# Revit family: IS_Conca_A7375_BIM_GB
name_source: partatom
category: Plumbing Fixtures
revit_build: Autodesk Revit 2017 (Build: 20160225_1515(x64)
units: mm (PartAtom-declared; Revit-internal decimal feet)

## family parameters
Always vertical = No
Cut with Voids When Loaded = No
OmniClass Number = 23.45.55.17
OmniClass Title = Mixing Faucets
Part Type = Normal
Room Calculation Point = No
Round Connector Dimension = Use Diameter
Shared = No
Work Plane-Based = No

## types (4) — shared parameters
Accessories = https://www.idealspec.co.uk
AreaUnits = millimeters
AssetType = Fixed
BIMobject category = Sanitary: Taps & Mixer
BarCode = 3800861085782
Brand = Ideal Standard
Brand url = http://www.idealstandard.co.uk
ConnectionType = Plumbing
CurrencyUnit = £
CurrentRevision = 1
Date of publishing = 22/09/2020
Edition number = 1
ExpectedLife = 30
FaucetFunction = UNSET
FaucetOperation = OTHER
FaucetType = OTHER
FlushRate = 0.00 m³
GTIN code = https://3800861085782
Help = https://www.idealspec.co.uk
IFC Classification = Sanitary Terminal
IfcExportAs = IfcValveType
IfcExportType = FAUCET
Installation instructions = https://www.idealspec.co.uk
InstallationInstructions = https://www.idealspec.co.uk
IsBuiltIn = No
IsHighPressure = No
IsSingleFlush = No
LinearUnits = millimeters
MaintenanceInformation = https://www.idealspec.co.uk
Manufacturer = Ideal Standard (UK) Ltd
Manufacturer name = Ideal Standard
ManufacturerURL = https://www.idealspec.co.uk
Material = Brass
Material main = Brass
NettWeight = 1,46 KG
NominalDepth = 82 mm
NominalHeight = 197 mm
NominalLength = 82 mm
NominalWidth = 163 mm  [stored 0.534777 ft]
Product Guid = 17384bdf-9aea-46d6-8c05-e0d8ab46731d
Product SKU = A7375
Product certification = https://www.idealspec.co.uk
Product data url = https://bimobject.com
Product family = Conca
Product group = BATH-SHOWER MIXERS
Product name = CONCA BSH MXR BIN DVGW KIT2/EASYB BR GUN
Product url = https://www.idealstandard.co.uk
ProductInformation = https://www.idealspec.co.uk
QR code = http://bimobject.com
Shape = Cylindrical
Size = 163 x 82 x 197 mm
Space = Internal
SpareParts = https://fastpart-spares.co.uk
Technical description = https://www.idealspec.co.uk
TestPressure = 10 Bar
UNSPSC Code = 301815
URL = https://www.idealspec.co.uk
Uniclass 1.4 Code = L725111
Uniclass 1.4 Description = Mixer taps
Uniclass2015Version = v1.1
Version = 1
VolumeUnits = Litres
WRASURL = https://www.wras.co.uk
WarrantyDescription = Manufacturers Warranty
WarrantyDurationParts = 5
WarrantyDurationUnit = year
WarrantyGuarantorParts = https://www.idealspec.co.uk
zero-valued in all types: FlushingRate, InletConnectionSize, MaterialThickness, OutletConnectionSize

## per-type parameters (varying)
| type | BIMObjectName | Color | Description | Features | Finish | MainColor | Model | ModelNumber | ModelReference | NBS Reference Code | NBS Reference Description | Name | Uniclass 2.0 Code | Uniclass 2.0 Description | Uniclass 2015 Code | Uniclass 2015 Name | Uniclass2015Code | Uniclass2015Title | Uniformat II Code | Uniformat II Description |
| A7375AA - CONCA BSH MXR BIN DVGW KIT2/EASY-BOX CHR | IS_IdealStandard_BathTaps_Conca_A7375 | Chrome | Conca Single Lever built in bath shower mixer - With additional back-flow prevention on second outlet. Requires built in kit A1000NU and a suitable outlet. | Single lever built in bath shower mixer - With additional back-flow prevention on second outlet. Requires built in kit A1000NU and a suitable outlet. | Chrome | Chrome | A7375AA | A7375AA | Single lever built in bath shower mixer - With additional back-flow prevention on second outlet. Requires built in kit A1000NU and a suitable outlet. | 45-35-70/315 | Water supply fittings for baths | BathTaps_Conca_A7375_IdealStandard | Pr_40_30_96_09 | Bath Taps | Pr_40_20_87_09 | Bath taps | Pr_40_20_87_09 | Bath taps | Pr_40_30_96_09 | Bath Taps |
| A7375A2 - CONCA BSH MXR BIN DVGW KIT2/EASYB BR GOLD | IS_IdealStandard_ShowerManualWaterSupplySets_Conca_A7375 | Brushed gold | Conca Single Lever built in shower mixer - Requires built in kit A1300NU and a suitable outlet. | Single lever built in shower mixer - Requires built in kit A1300NU and a suitable outlet. | Brushed gold | Brushed gold | A7375A2 | A7375A2 | Single lever built in shower mixer - Requires built in kit A1300NU and a suitable outlet. | 45-35-70/335 | Shower mixers | ShowerManualWaterSupplySets_Conca_A7375_IdealStandard | Pr_40_30_96_78 | Shower Manual Water Supply Sets | Pr_40_20_87_78 | Shower manual water supply sets | Pr_40_20_87_78 | Shower manual water supply sets | Pr_40_30_96_78 | Shower Manual Water Supply Sets |
| A7375A5 - CONCA BSH MXR BIN DVGW KIT2/EASYB M GREY | IS_IdealStandard_ShowerManualWaterSupplySets_Conca_A7375 | Brushed Gun metal | Conca Single Lever built in shower mixer - Requires built in kit A1300NU and a suitable outlet. | Single lever built in shower mixer - Requires built in kit A1300NU and a suitable outlet. | Brushed Gun metal | Brushed Gun metal | A7375A5 | A7375A5 | Single lever built in shower mixer - Requires built in kit A1300NU and a suitable outlet. | 45-35-70/335 | Shower mixers | ShowerManualWaterSupplySets_Conca_A7375_IdealStandard | Pr_40_30_96_78 | Shower Manual Water Supply Sets | Pr_40_20_87_78 | Shower manual water supply sets | Pr_40_20_87_78 | Shower manual water supply sets | Pr_40_30_96_78 | Shower Manual Water Supply Sets |
| A7375GN - CONCA BSH MXR BIN DVGW KIT2/EASYB SILVER STORM | IS_IdealStandard_ShowerManualWaterSupplySets_Conca_A7375 | Brushed nickel | Conca Single Lever built in shower mixer - Requires built in kit A1300NU and a suitable outlet. | Single lever built in shower mixer - Requires built in kit A1300NU and a suitable outlet. | Brushed nickel | Brushed nickel | A7375GN | A7375GN | Single lever built in shower mixer - Requires built in kit A1300NU and a suitable outlet. | 45-35-70/335 | Shower mixers | ShowerManualWaterSupplySets_Conca_A7375_IdealStandard | Pr_40_30_96_78 | Shower Manual Water Supply Sets | Pr_40_20_87_78 | Shower manual water supply sets | Pr_40_20_87_78 | Shower manual water supply sets | Pr_40_30_96_78 | Shower Manual Water Supply Sets |

note: [stored X ft] marks values corroborated as IEEE doubles in the binary element streams (Revit-internal decimal feet)

## geometry (parser evidence)
native form markers: Sweep x3
no freeform markers — native parametric forms only
